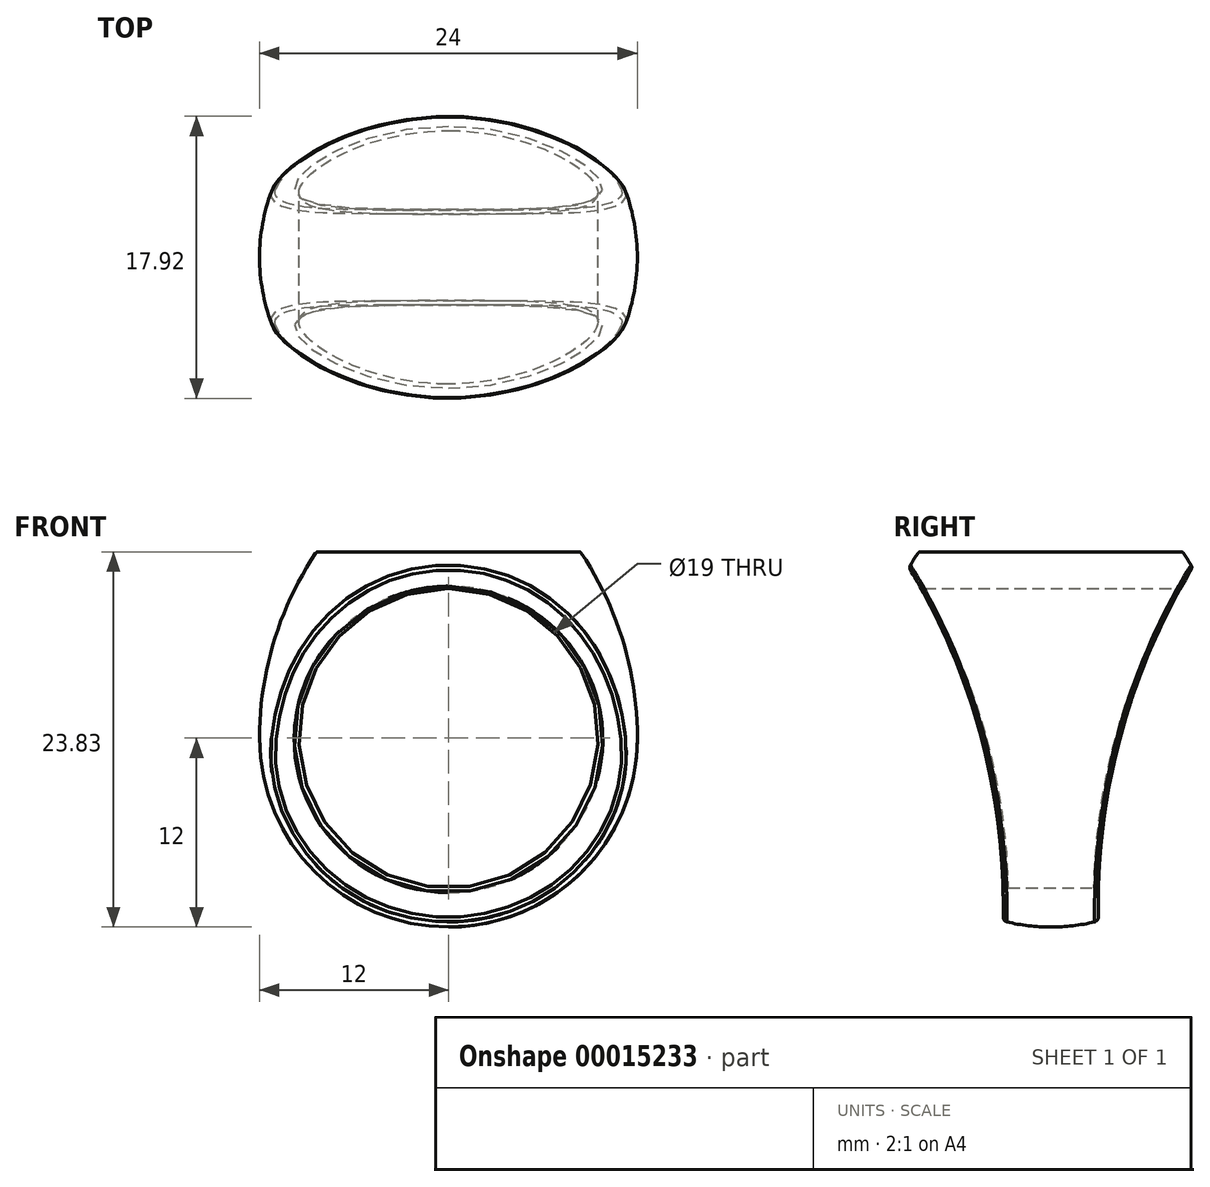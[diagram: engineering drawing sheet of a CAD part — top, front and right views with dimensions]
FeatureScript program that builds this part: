
annotation { "Feature Type Name" : "Feature", "Feature Type Description" : "" }
export const myFeature = defineFeature(function(context is Context, id is Id, definition is map)
    precondition{}
    {
        {
            var Q0;
            Q0=qCreatedBy(makeId("Front.planeOp"),FACE);
            var sketch = newSketch(context, id + "F0", { "sketchPlane" : qUnion([Q0])});
            skCircle(sketch, "E0", {"center": v(0, 0) * mm, "radius": 9.5 * mm});
            skArc(sketch, "E1.0", {"start": v(-12, 0) * mm, "mid": v(0, -12) * mm, "end": v(12, 0) * mm});
            skLineSegment(sketch, "E2", {"start": v(0, 11.83) * mm, "end": v(-8.38, 11.83) * mm});
            skArc(sketch, "E3", {"start": v(-8.38, 11.83) * mm, "mid": v(-11.08, 6.18) * mm, "end": v(-12, 0) * mm});
            skLineSegment(sketch, "E4.MirrorCS", {"start": v(0, 11.83) * mm, "end": v(8.38, 11.83) * mm});
            skArc(sketch, "E5.MirrorCS", {"start": v(8.38, 11.83) * mm, "mid": v(11.08, 6.18) * mm, "end": v(12, 0) * mm});
            skLineSegment(sketch, "E6", {"start": v(0, 11.83) * mm, "end": v(0, 16.77) * mm});
            skLineSegment(sketch, "E7", {"start": v(0, 16.77) * mm, "end": v(43.3, 16.77) * mm});
            skLineSegment(sketch, "E8", {"start": v(43.3, 16.77) * mm, "end": v(43.3, -18.41) * mm});
            skLineSegment(sketch, "E9", {"start": v(43.3, -18.41) * mm, "end": v(0, -18.41) * mm});
            skLineSegment(sketch, "E10", {"start": v(0, -18.41) * mm, "end": v(0, -12) * mm});
            skSolve(sketch);
        }
        {
            var Q0;
            Q0=makeQuery(id+"F0.imprint","IMPRINT",FACE,{"disambiguationData":[TD([[makeQuery(id+"F0.imprint","IMPRINT",EDGE,{"derivedFrom":sQuery(id+"F0.wireOp",EDGE,"E0")}),-1.0]])]});
            extrude(context, id + "F1", {"entities" : qUnion([Q0]), "depth" : 25 * mm, "symmetric" : true});
        }
        {
            var Q0;
            Q0=makeQuery(id+"F0.imprint","IMPRINT",FACE,{"disambiguationData":[TD([[makeQuery(id+"F0.imprint","IMPRINT",EDGE,{"derivedFrom":sQuery(id+"F0.wireOp",EDGE,"E4.MirrorCS")}),1.0]])]});
            var Q1;
            Q1=sQuery(id+"F0.wireOp",EDGE,"E6");
            revolve(context, id + "F2", {"operationType" : NewBodyOperationType.REMOVE, "entities" : qUnion([Q0]), "axis" : qUnion([Q1]), "revolveType" : RevolveType.FULL, "oppositeDirection" : true});
        }
        {
            var Q0;
            Q0=qCreatedBy(makeId("Right.planeOp"),FACE);
            var sketch = newSketch(context, id + "F3", { "sketchPlane" : qUnion([Q0])});
            skArc(sketch, "E11", {"start": v(-3.35, -15.9) * mm, "mid": v(-4.44, 0.15) * mm, "end": v(-11.55, 14.58) * mm});
            skLineSegment(sketch, "E12", {"start": v(-11.55, 14.58) * mm, "end": v(-11.55, -15.9) * mm});
            skLineSegment(sketch, "E13", {"start": v(-11.55, -15.9) * mm, "end": v(-3.35, -15.9) * mm});
            skLineSegment(sketch, "E14.MirrorCS", {"start": v(11.55, 14.58) * mm, "end": v(11.55, -15.9) * mm});
            skLineSegment(sketch, "E15.MirrorCS", {"start": v(11.55, -15.9) * mm, "end": v(3.35, -15.9) * mm});
            skArc(sketch, "E16.MirrorCS", {"start": v(3.35, -15.9) * mm, "mid": v(4.44, 0.15) * mm, "end": v(11.55, 14.58) * mm});
            skSolve(sketch);
        }
        {
            var Q0;
            Q0=makeQuery(id+"F3.imprint","IMPRINT",FACE,{"disambiguationData":[TD([[makeQuery(id+"F3.imprint","IMPRINT",EDGE,{"derivedFrom":sQuery(id+"F3.wireOp",EDGE,"E11")}),1.0]])]});
            var Q1;
            Q1=makeQuery(id+"F3.imprint","IMPRINT",FACE,{"disambiguationData":[TD([[makeQuery(id+"F3.imprint","IMPRINT",EDGE,{"derivedFrom":sQuery(id+"F3.wireOp",EDGE,"E14.MirrorCS")}),-1.0]])]});
            extrude(context, id + "F4", {"entities" : qUnion([Q0, Q1]), "operationType" : NewBodyOperationType.REMOVE, "oppositeDirection" : true, "depth" : 40.7 * mm, "symmetric" : true});
        }
        {
            var Q0;
            Q0=makeQuery(id+"F4.boolean.opBoolean","INTERSECT",EDGE,{"derivedFrom":[makeQuery(id+"F1.opExtrude","SWEPT_FACE",FACE,{"disambiguationData":[OSD([sQuery(id+"F0.wireOp",EDGE,"E0")])]}),makeQuery(id+"F4.opExtrude","SWEPT_FACE",FACE,{"disambiguationData":[OSD([sQuery(id+"F3.wireOp",EDGE,"E16.MirrorCS")])]})]});
            fillet(context, id + "F5", {"entities" : qUnion([Q0]), "radius" : .3 * mm, "tangentPropagation" : true, "allowEdgeOverflow" : false});
        }
        {
            var Q0;
            Q0=makeQuery(id+"F4.boolean.opBoolean","INTERSECT",EDGE,{"derivedFrom":[makeQuery(id+"F2.boolean.opBoolean","COPY",FACE,{"derivedFrom":makeQuery(id+"F2.opRevolve","SWEPT_FACE",FACE,{"disambiguationData":[OSD([sQuery(id+"F0.wireOp",EDGE,"E1.0")])]})}),makeQuery(id+"F4.opExtrude","SWEPT_FACE",FACE,{"disambiguationData":[OSD([sQuery(id+"F3.wireOp",EDGE,"E16.MirrorCS")])]})]});
            var Q1;
            Q1=makeQuery(id+"F4.boolean.opBoolean","INTERSECT",EDGE,{"derivedFrom":[makeQuery(id+"F2.boolean.opBoolean","COPY",FACE,{"derivedFrom":makeQuery(id+"F2.opRevolve","SWEPT_FACE",FACE,{"disambiguationData":[OSD([sQuery(id+"F0.wireOp",EDGE,"E5.MirrorCS")])]})}),makeQuery(id+"F4.opExtrude","SWEPT_FACE",FACE,{"disambiguationData":[OSD([sQuery(id+"F3.wireOp",EDGE,"E16.MirrorCS")])]})]});
            fillet(context, id + "F6", {"entities" : qUnion([Q0, Q1]), "radius" : .3 * mm, "tangentPropagation" : true, "allowEdgeOverflow" : false});
        }
        {
            var Q0;
            Q0=makeQuery(id+"F4.boolean.opBoolean","COPY",FACE,{"derivedFrom":makeQuery(id+"F4.opExtrude","SWEPT_FACE",FACE,{"disambiguationData":[OSD([sQuery(id+"F3.wireOp",EDGE,"E11")])]})});
            fillet(context, id + "F7", {"entities" : qUnion([Q0]), "radius" : .3 * mm, "tangentPropagation" : true, "allowEdgeOverflow" : false});
        }
        {
            var Q0;
            Q0=makeQuery(id+"F1.opExtrude","SWEPT_FACE",FACE,{"disambiguationData":[OSD([sQuery(id+"F0.wireOp",EDGE,"E2"),sQuery(id+"F0.wireOp",EDGE,"E4.MirrorCS")])]});
            fillet(context, id + "F8", {"entities" : qUnion([Q0]), "radius" : .15 * mm, "tangentPropagation" : true, "allowEdgeOverflow" : false});
        }
    });
